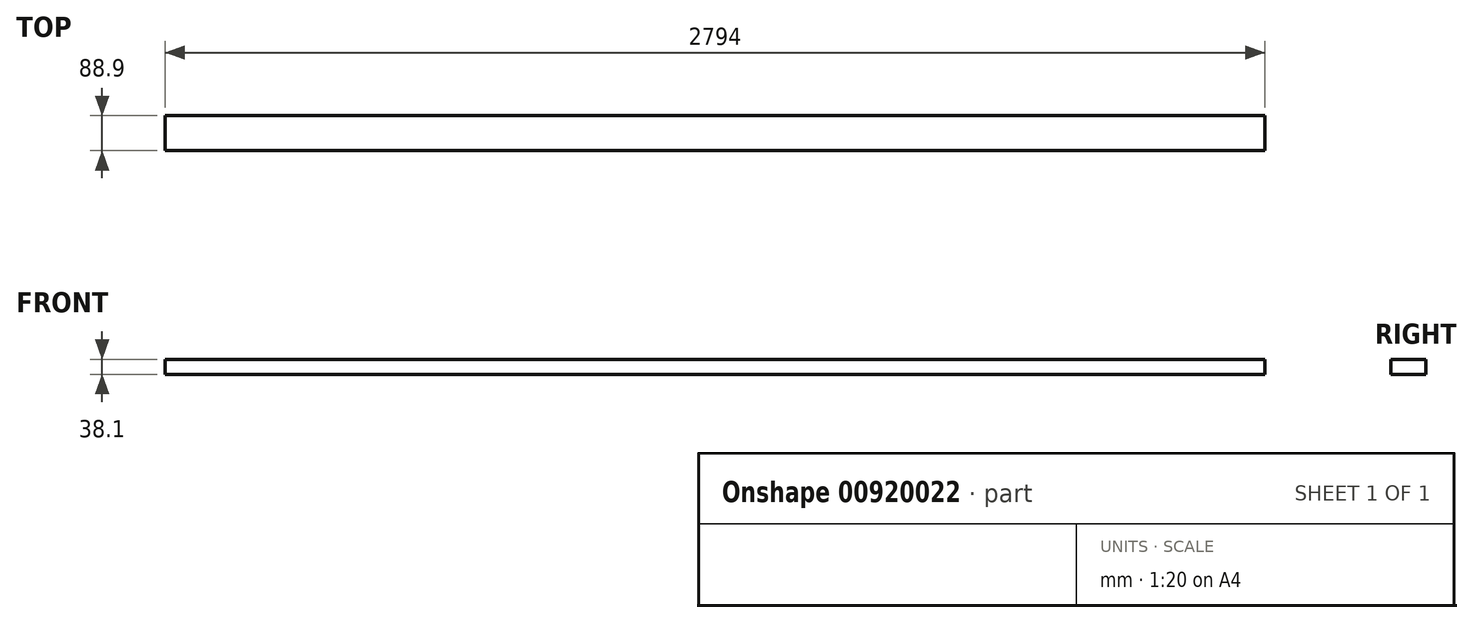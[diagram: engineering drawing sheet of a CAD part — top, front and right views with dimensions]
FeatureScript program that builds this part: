
annotation { "Feature Type Name" : "Feature", "Feature Type Description" : "" }
export const myFeature = defineFeature(function(context is Context, id is Id, definition is map)
    precondition{}
    {
        {
            var Q0;
            Q0=qCreatedBy(makeId("Right.planeOp"),FACE);
            var sketch = newSketch(context, id + "F0", { "sketchPlane" : qUnion([Q0])});
            skLineSegment(sketch, "E0.bottom", {"start": v(44.45, -19.05) * mm, "end": v(-44.45, -19.05) * mm});
            skLineSegment(sketch, "E0.top", {"start": v(44.45, 19.05) * mm, "end": v(-44.45, 19.05) * mm});
            skLineSegment(sketch, "E0.left", {"start": v(44.45, -19.05) * mm, "end": v(44.45, 19.05) * mm});
            skLineSegment(sketch, "E0.right", {"start": v(-44.45, -19.05) * mm, "end": v(-44.45, 19.05) * mm});
            skPoint(sketch, "E0.middle", {"position": v(0, 0) * mm});
            skSolve(sketch);
        }
        {
            var Q0;
            Q0=makeQuery(id+"F0.imprint","IMPRINT",FACE,{"disambiguationData":[TD([[makeQuery(id+"F0.imprint","IMPRINT",EDGE,{"derivedFrom":sQuery(id+"F0.wireOp",EDGE,"E0.bottom")}),-1.0]])]});
            extrude(context, id + "F1", {"entities" : qUnion([Q0]), "oppositeDirection" : true, "depth" : 2794 * mm, "offsetDistance" : 25.4 * mm});
        }
    });
